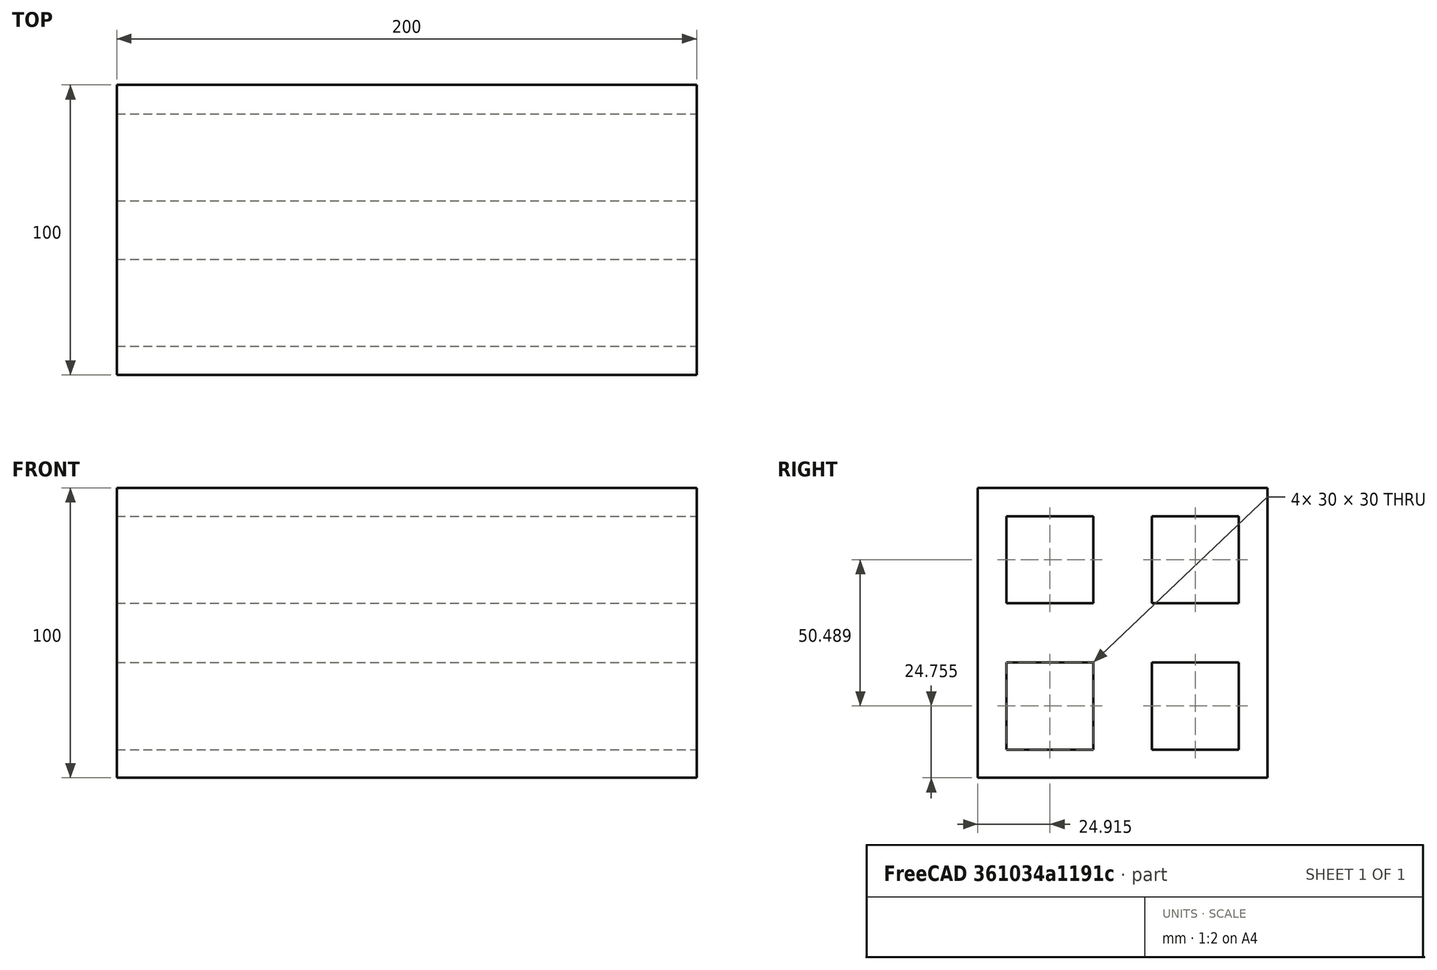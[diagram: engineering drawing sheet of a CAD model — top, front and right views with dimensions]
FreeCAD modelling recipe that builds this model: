
FCSTD DOCUMENT  (FreeCAD 0.21R33694 (Git))
Label: OJT1_T18R01_ladrillo
License: All rights reserved
LicenseURL: http://en.wikipedia.org/wiki/All_rights_reserved
objects: Sketcher::SketchObject×1, PartDesign::Pad×1, PartDesign::Body×1
note: 4 computed .brp shape members not serialized (recipe doc carries the construction recipe); baked Part::Feature solids carry a one-line shape summary decoded from their .brp

FEATURE [Sketcher::SketchObject] Sketch
  FullyConstrained = false
  MapMode = 5
  Support = -> [XY_Plane]
  sketch-geometry (20):
    g0: LineSegment StartX=-50 StartY=50 StartZ=0 EndX=50 EndY=50 EndZ=0
    g1: LineSegment StartX=50 StartY=50 StartZ=0 EndX=50 EndY=-50 EndZ=0
    g2: LineSegment StartX=50 StartY=-50 StartZ=0 EndX=-50 EndY=-50 EndZ=0
    g3: LineSegment StartX=-50 StartY=-50 StartZ=0 EndX=-50 EndY=50 EndZ=0
    g4: LineSegment StartX=-40.2447 StartY=40.0848 StartZ=0 EndX=-10.2447 EndY=40.0848 EndZ=0
    g5: LineSegment StartX=-10.2447 StartY=40.0848 StartZ=0 EndX=-10.2447 EndY=10.0848 EndZ=0
    g6: LineSegment StartX=-10.2447 StartY=10.0848 StartZ=0 EndX=-40.2447 EndY=10.0848 EndZ=0
    g7: LineSegment StartX=-40.2447 StartY=10.0848 StartZ=0 EndX=-40.2447 EndY=40.0848 EndZ=0
    g8: LineSegment StartX=-40.2447 StartY=-10.0848 StartZ=0 EndX=-10.2447 EndY=-10.0848 EndZ=0
    g9: LineSegment StartX=-10.2447 StartY=-10.0848 StartZ=0 EndX=-10.2447 EndY=-40.0848 EndZ=0
    g10: LineSegment StartX=-10.2447 StartY=-40.0848 StartZ=0 EndX=-40.2447 EndY=-40.0848 EndZ=0
    g11: LineSegment StartX=-40.2447 StartY=-40.0848 StartZ=0 EndX=-40.2447 EndY=-10.0848 EndZ=0
    g12: LineSegment StartX=10.2447 StartY=40.0848 StartZ=0 EndX=40.2447 EndY=40.0848 EndZ=0
    g13: LineSegment StartX=40.2447 StartY=40.0848 StartZ=0 EndX=40.2447 EndY=10.0848 EndZ=0
    g14: LineSegment StartX=40.2447 StartY=10.0848 StartZ=0 EndX=10.2447 EndY=10.0848 EndZ=0
    g15: LineSegment StartX=10.2447 StartY=10.0848 StartZ=0 EndX=10.2447 EndY=40.0848 EndZ=0
    g16: LineSegment StartX=10.2447 StartY=-10.0848 StartZ=0 EndX=40.2447 EndY=-10.0848 EndZ=0
    g17: LineSegment StartX=40.2447 StartY=-10.0848 StartZ=0 EndX=40.2447 EndY=-40.0848 EndZ=0
    g18: LineSegment StartX=40.2447 StartY=-40.0848 StartZ=0 EndX=10.2447 EndY=-40.0848 EndZ=0
    g19: LineSegment StartX=10.2447 StartY=-40.0848 StartZ=0 EndX=10.2447 EndY=-10.0848 EndZ=0
  constraints (52):
    c: Coincident(g0,g1)
    c: Coincident(g1,g2)
    c: Coincident(g2,g3)
    c: Coincident(g3,g0)
    c: Symmetric(g0,g0,g-2)
    c: Symmetric(g0,g1,g-1)
    c: Symmetric(g2,g1,g-2)
    c: DistanceX(g0,g0) = 100
    c: DistanceY(g1,g1) = 100
    c: Coincident(g4,g5)
    c: Coincident(g5,g6)
    c: Coincident(g6,g7)
    c: Coincident(g7,g4)
    c: Horizontal(g4)
    c: Horizontal(g6)
    c: Vertical(g5)
    c: Vertical(g7)
    c: Coincident(g8,g9)
    c: Coincident(g9,g10)
    c: Coincident(g10,g11)
    c: Coincident(g11,g8)
    c: Horizontal(g8)
    c: Horizontal(g10)
    c: Vertical(g9)
    c: Vertical(g11)
    c: Coincident(g12,g13)
    c: Coincident(g13,g14)
    c: Coincident(g14,g15)
    c: Coincident(g15,g12)
    c: Horizontal(g12)
    c: Horizontal(g14)
    c: Vertical(g13)
    c: Vertical(g15)
    c: Coincident(g16,g17)
    c: Coincident(g17,g18)
    c: Coincident(g18,g19)
    c: Coincident(g19,g16)
    c: Horizontal(g16)
    c: Horizontal(g18)
    c: Vertical(g17)
    c: Vertical(g19)
    c: DistanceX(g4,g4) = 30
    c: DistanceY(g7,g7) = 30
    c: DistanceX(g8,g8) = 30
    c: DistanceY(g11,g11) = 30
    c: DistanceX(g12,g12) = 30
    c: DistanceY(g13,g13) = 30
    c: DistanceX(g16,g16) = 30
    c: DistanceY(g17,g17) = 30
    c: Symmetric(g12,g4,g-2)
    c: Symmetric(g5,g8,g-1)
    c: Symmetric(g8,g16,g-2)
FEATURE [PartDesign::Pad] Pad
  Direction = (0,0,1)
  Length = 200
  Length2 = 10
  Profile = -> Sketch
  ReferenceAxis = -> Sketch [N_Axis]
  Type = 0
FEATURE [PartDesign::Body] Body
  Group = -> [Sketch,Pad]
  Origin = -> Origin
  Placement = pos=(0,0,0) rot=(0,1,0;1.5708rad)
  Tip = -> Pad
